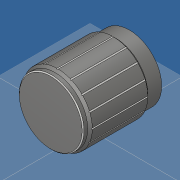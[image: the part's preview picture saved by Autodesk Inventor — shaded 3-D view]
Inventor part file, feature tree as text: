
AUTODESK INVENTOR PART (.ipt)
format: ipt  version: 2019 (Build 230136000, 136)  size: 212,992 bytes
history: native  units: mm
features: extrude x3, chamfer x2, sketch x1
ambient origin geometry x8: Origin, YZ Plane, XZ Plane, XY Plane, X Axis, Y Axis, Z Axis, Center Point
bodies: Volumenkörper1 (feature_tree)
feature tree (6):
  sketch  "Skizze1"  dims[d0=15.0mm d1=17.0mm d2=0.0mm d3=14.0mm d4=7.0mm d5=5.0mm d6=0.0mm d7=0.0mm d8=0.5mm d9=2.0mm d10=45.0deg d11=0.2mm d12=2.0mm d13=45.0deg d14=6.0mm d15=1.5mm d16=8.5mm d17=0.0mm d18=0.0mm d20=0.3mm d21=0.1mm d22=160.0mm d24=360.0deg]
  extrude  "Extrusion1"  Depth=17.0mm TaperAngle=0.0deg
  extrude  "Extrusion2"  Depth=8.5mm
  chamfer  "Fase1"  Distance=7.0mm
  chamfer  "Fase2"  Distance=0.5mm Angle=45.0deg
  extrude  "Extrusion3"  Depth=8.5mm TaperAngle=45.0deg
